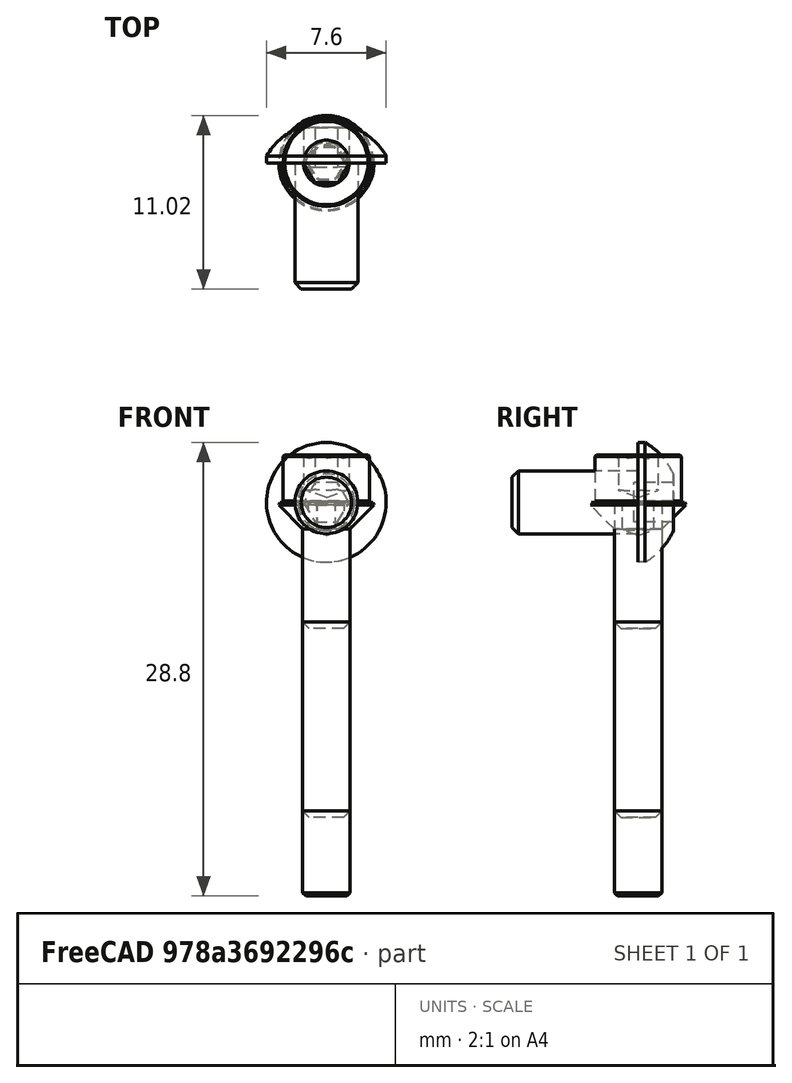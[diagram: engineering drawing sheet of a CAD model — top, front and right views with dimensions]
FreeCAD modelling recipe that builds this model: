
FCSTD DOCUMENT  (FreeCAD 0.14R3692 (Git))
Label: bolts
License: CC-BY 3.0
LicenseURL: http://creativecommons.org/licenses/by/3.0/
objects: Part::Feature×5, Sketcher::SketchObject×1, PartDesign::Pocket×1
note: 8 computed .brp shape members not serialized (recipe doc carries the construction recipe); baked Part::Feature solids carry a one-line shape summary decoded from their .brp

FEATURE [Part::Feature] Part__Feature  label="bolt-m4x8-bhcs-orig"
  shape: bbox 7.613 x 10.62 x 7.622 mm, 14 faces (baked)
FEATURE [Sketcher::SketchObject] Sketch  label="hex-2.5-sketch"
  Placement = pos=(0,2.24,0) rot=(0,0.707107,0.707107;3.14159rad)
  Support = -> Part__Feature [Face11]
  sketch-geometry (7):
    g0: Circle [constr] CenterX=0 CenterY=0 CenterZ=0 NormalX=0 NormalY=0 NormalZ=1 Radius=1.44338
    g1: LineSegment StartX=-0.721688 StartY=1.25 StartZ=0 EndX=0.721688 EndY=1.25 EndZ=0
    g2: LineSegment StartX=0.721688 StartY=1.25 StartZ=0 EndX=1.44338 EndY=0 EndZ=0
    g3: LineSegment StartX=1.44338 StartY=0 StartZ=0 EndX=0.721688 EndY=-1.25 EndZ=0
    g4: LineSegment StartX=0.721688 StartY=-1.25 StartZ=0 EndX=-0.721688 EndY=-1.25 EndZ=0
    g5: LineSegment StartX=-0.721688 StartY=-1.25 StartZ=0 EndX=-1.44338 EndY=0 EndZ=0
    g6: LineSegment StartX=-1.44338 StartY=0 StartZ=0 EndX=-0.721688 EndY=1.25 EndZ=0
  constraints (20):
    c: Coincident(g0,g-1)
    c: Coincident(g1,g2)
    c: Coincident(g2,g3)
    c: Coincident(g3,g4)
    c: Coincident(g4,g5)
    c: Coincident(g5,g6)
    c: Coincident(g6,g1)
    c: PointOnObject(g1,g0)
    c: PointOnObject(g1,g0)
    c: PointOnObject(g2,g0)
    c: PointOnObject(g3,g0)
    c: PointOnObject(g4,g0)
    c: PointOnObject(g5,g0)
    c: Equal(g2,g1)
    c: Equal(g1,g6)
    c: Equal(g6,g5)
    c: Equal(g5,g4)
    c: Equal(g4,g3)
    c: Horizontal(g4)
    c: DistanceY(g1,g3) = -2.5
FEATURE [PartDesign::Pocket] Pocket  label="hex-2.5-pocket"
  Length = 2.5
  Sketch = -> Sketch
  Type = 0
FEATURE [Part::Feature] Pocket001  label="bolt-m4x8-bhcs"
  shape: bbox 7.613 x 10.62 x 7.622 mm, 14 faces (baked)
FEATURE [Part::Feature] Part__Feature001  label="bolt-m3x20-hshcs"
  shape: bbox 5.5 x 5.5 x 23 mm, 16 faces (baked)
FEATURE [Part::Feature] Part__Feature002  label="bolt-m3x8-hshcs"
  shape: bbox 5.5 x 5.5 x 11 mm, 16 faces (baked)
FEATURE [Part::Feature] Part__Feature003  label="bolt-m3x25-hschs"
  shape: bbox 6.046 x 6.046 x 25 mm, 26 faces (baked)
